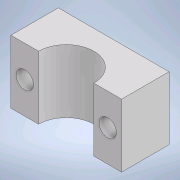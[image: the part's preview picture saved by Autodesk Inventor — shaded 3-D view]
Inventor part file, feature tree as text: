
AUTODESK INVENTOR PART (.ipt)
format: ipt  version: 2020.1 (Build 241239000, 239)  size: 107,008 bytes
history: native  units: mm
features: sketch x3, extrude x2, hole x1
ambient origin geometry x8: Origin, YZ Plane, XZ Plane, XY Plane, X Axis, Y Axis, Z Axis, Center Point
bodies: Volumenkörper1 (feature_tree)
feature tree (6):
  extrude  "Extrusion1"  Depth=30.0mm
  extrude  "Extrusion2"  Depth=40.0mm
  hole  "Bohrung1"  [1 undecoded]
  sketch  "Skizze1"  dims[d0=70.0mm d1=30.0mm]
  sketch  "Skizze2"  dims[d2=40.0mm d3=0.0mm d4=35.0mm]
  sketch  "Skizze4"  dims[d5=40.0mm d6=0.0mm d12=11.0mm d13=6.0mm d14=4.0mm d15=2.0mm d16=90.0deg d17=30.0mm d18=20.594885mm]
note: 1 required parameter value undecoded (feature->parameter linkage not recoverable at this tier; creation-order binding heuristic only, values carry confidence <= 0.55)
